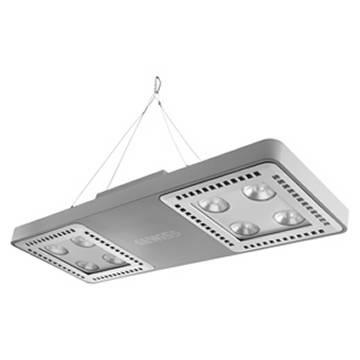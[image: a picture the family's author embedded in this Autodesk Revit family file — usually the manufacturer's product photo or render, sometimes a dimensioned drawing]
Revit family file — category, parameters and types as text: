
# Revit family: Lighting-Industrial-GEWISS-SMART[4]HE_HIGHBAYS-LED_2M
name_source: partatom
category: Apparecchi per illuminazione
units: mm (PartAtom-declared; Revit-internal decimal feet)

## family parameters
Basato su piano di lavoro = Sì
Condiviso = No
Numero OmniClass = 23.80.70.00
Punto di calcolo locali = No
Quota connettore circolare = Usa diametro
Sempre verticale = No
Sorgente d'illuminazione = No
Taglio con vuoti quando caricato = No
Tipo di parte = Normale
Titolo OmniClass = Lighting

## types (36) — shared parameters
Application = Internal
Body = PA6 "Halogen Free" loaded fibreglass
Carico apparente = 97 VA
Catalogue = LIGHTING
Classification: = -
Classificazione = Lighting
Color Rendering Index = CRI-80
Colour = Grey RAL 7035
Colour : = Grey RAL 7035
Commenti sul wattaggio = 97W
Context = Lighting for industries and sports facilities
Control System = ON / OFF
Control System : = ON / OFF
DIN 18032-3 certification = With Bracket - Rope Kit + terminal&nbsp;(in approval)
Device with reduced surface temperature = Yes
Dist_sorg_lum = 10 mm  [stored 0.0328084 ft]
Driver = Included
Driver Box = Built-in
Electrocod = 2444
Eletrical and lighting features = -
External screw = Stainless steel
Fixing = -
Gasket = anti-aging silicone
General information = -
Glow Wire Test : = 850 °C
IDF = 024dbe20-8244-495a-a889-af2c2a435427
IDT = 170d63836ef34e7a91627e9879a3eea4
IP degree = IP66
IPEA = -
Immagine tipo = GWL1311.jpg
Installationa and maintenance = -
Insulation class = I
LED Maintenance = Non-replaceable
Lampada = LED
Larghezza = 254 mm
Lifetime = L90B10 (Tq+25°C) = 70.000 h - L90B10 (Tq+50°C) = 35.000 h
Locking Hook = -
Luminaire = LED Industrial ReflectorÂ
Lunghezza = 699 mm  [stored 2.29331 ft]
Mascherina = <Per categoria>
Materials = -
Maximum surface exposed to the wind : = 0,184 m²
Motore = <Per categoria>
Mouting and installation = Ceiling - Wallmounting - Suspension
Operating temperature : = -30°C ÷ +50 °C
Optic Maintenance = Non-replaceable
Optic and illuminating features = -
Overvoltage protection = DM 6kV / CM 6kV
Photobiological Risk Class = RG0
Produttore = GEWISS S.p.A.
Prospetto di default = 1219 mm
Rated frequency (Hz) = 50/60 Hz
Shield type = Tempered glass Thickness 4mm
Shock resistance = IK08
Spessore plafoniera = 40 mm  [stored 0.131234 ft]
Standard Deviation Colour Matching = SDCM = 3
Standard- = EN 60598-1 ; EN 60598-2-1 ; EN 60598-2-24
Standards and approvals = -
Stocking temperature = -40 +70 °C
Struttura plafoniera = <Per categoria>
Supply voltage = 220 - 240 V
System power = 95W
Technical sheet = https://www.gewiss.com
Tilt- = With bracket accessory
Trasformatore = <Per categoria>
Type of light source = LED - Not replaceable
URL = https://www.gewiss.com
Unique digital code (Datamatrix) = Datamatrix
Version file RFA = 20.11
Voltaggio = 230 V
Warranty = 5 years
Weight (kg): = 6,5
Wiring = With GW connect watertight connector

## per-type parameters (varying)
| type | Colour temperature | Descrizione | Efficiency (lm/W) | Lumen output (lm) | Modello | Optic | Optic : | SEO | Unified Glare Rating |
| GWS4220AF830 - SMART4HB 2M ST.AL.ON/OFF 30° 30K | 3000K | SMART[4]HB 2M ST.AL.ON/OFF 30° 30K | 137 | 13000 | GWS4220AF830 | 30° | Metallic PC reflector and PMMA lenses |  | UGR - 19 |
| GWS4222AC830 - SMART4HB 2M C.PAS.ON/OFF ASI.30K | 3000K | SMART[4]HB 2M C.PAS.ON/OFF ASI.30K | 125 | 11900 | GWS4222AC830 | Asymmetrical | Metallic PC reflector and PMMA lenses | High bay | - |
| GWS4222AC840 - SMART4HB 2M C.PAS.ON/OFF ASI.40K | 4000K | SMART[4]HB 2M C.PAS.ON/OFF ASI.40K | 132 | 12500 | GWS4222AC840 | Asymmetrical | Metallic PC reflector and PMMA lenses | High bay | - |
| GWS4220AP840 - SMART4HB 2M ST.AL.ON/OFF 90° 40K | 4000K | SMART[4]HB 2M ST.AL.ON/OFF 90° 40K | 146 | 13900 | GWS4220AP840 | 90° | Metallic PC reflector and PMMA lenses |  | UGR - 22 |
| GWS4220AH840 - SMART4HB 2M ST.AL.ON/OFF 60° 40K | 4000K | SMART[4]HB 2M ST.AL.ON/OFF 60° 40K | 145 | 13800 | GWS4220AH840 | 60° | Metallic PC reflector and PMMA lenses |  | UGR - 22 |
| GWS4220AC840 - SMART4HB 2M ST.AL.ON/OFF ASI.40K | 4000K | SMART[4]HB 2M ST.AL.ON/OFF ASI.40K | 132 | 12500 | GWS4220AC840 | Asymmetrical | Metallic PC reflector and PMMA lenses | High bay | - |
| GWS4222AA830 - SMART4HB 2M C.PAS.ON/OFF ARR.30K | 3000K | SMART[4]HB 2M C.PAS.ON/OFF ARR.30K | 139 | 13200 | GWS4222AA830 | Array | Metallized polycarbonate reflector |  | UGR - 25 |
| GWS4222AQ830 - SMART4HB 2M C.PAS.ON/OFF ELL.30K | 3000K | SMART[4]HB 2M C.PAS.ON/OFF ELL.30K | 124 | 11800 | GWS4222AQ830 | Elliptical | Metallic PC reflector and PMMA lenses | High bay | - |
| GWS4222AH830 - SMART4HB 2M C.PAS.ON/OFF 60° 30K | 3000K | SMART[4]HB 2M C.PAS.ON/OFF 60° 30K | 138 | 13100 | GWS4222AH830 | 60° | Metallic PC reflector and PMMA lenses |  | UGR - 22 |
| GWS4222AF840 - SMART4HB 2M C.PAS.ON/OFF 30° 40K | 4000K | SMART[4]HB 2M C.PAS.ON/OFF 30° 40K | 144 | 13700 | GWS4222AF840 | 30° | Metallic PC reflector and PMMA lenses |  | UGR - 19 |
| GWS4222AQ857 - SMART4HB 2M C.PAS.ON/OFF ELL.57K | 5700K | SMART[4]HB 2M C.PAS.ON/OFF ELL.57K | 129 | 12300 | GWS4222AQ857 | Elliptical | Metallic PC reflector and PMMA lenses | High bay | - |
| GWS4220AH830 - SMART4HB 2M ST.AL.ON/OFF 60° 30K | 3000K | SMART[4]HB 2M ST.AL.ON/OFF 60° 30K | 138 | 13100 | GWS4220AH830 | 60° | Metallic PC reflector and PMMA lenses |  | UGR - 22 |
| GWS4220AC830 - SMART4HB 2M ST.AL.ON/OFF ASI.30K | 3000K | SMART[4]HB 2M ST.AL.ON/OFF ASI.30K | 125 | 11900 | GWS4220AC830 | Asymmetrical | Metallic PC reflector and PMMA lenses | High bay | - |
| GWS4222AQ840 - SMART4HB 2M C.PAS.ON/OFF ELL.40K | 4000K | SMART[4]HB 2M C.PAS.ON/OFF ELL.40K | 129 | 12300 | GWS4222AQ840 | Elliptical | Metallic PC reflector and PMMA lenses | High bay | - |
| GWS4222AC857 - SMART4HB 2M C.PAS.ON/OFF ASI.57K | 5700K | SMART[4]HB 2M C.PAS.ON/OFF ASI.57K | 132 | 12500 | GWS4222AC857 | Asymmetrical | Metallic PC reflector and PMMA lenses | High bay | - |
| GWS4220AF840 - SMART4HB 2M ST.AL.ON/OFF 30° 40K | 4000K | SMART[4]HB 2M ST.AL.ON/OFF 30° 40K | 144 | 13700 | GWS4220AF840 | 30° | Metallic PC reflector and PMMA lenses |  | UGR - 19 |
| GWS4220AA830 - SMART4HB 2M ST.AL.ON/OFF ARR.30K | 3000K | SMART[4]HB 2M ST.AL.ON/OFF ARR.30K | 139 | 13200 | GWS4220AA830 | Array | Metallized polycarbonate reflector |  | UGR - 25 |
| GWS4220AP857 - SMART4HB 2M ST.AL.ON/OFF 90° 57K | 5700K | SMART[4]HB 2M ST.AL.ON/OFF 90° 57K | 146 | 13900 | GWS4220AP857 | 90° | Metallic PC reflector and PMMA lenses |  | UGR - 22 |
| GWS4222AH857 - SMART4HB 2M C.PAS.ON/OFF 60° 57K | 5700K | SMART[4]HB 2M C.PAS.ON/OFF 60° 57K | 145 | 13800 | GWS4222AH857 | 60° | Metallic PC reflector and PMMA lenses |  | UGR - 22 |
| GWS4220AQ857 - SMART4HB 2M ST.AL.ON/OFF ELL.57K | 5700K | SMART[4]HB 2M ST.AL.ON/OFF ELL.57K | 129 | 12300 | GWS4220AQ857 | Elliptical | Metallic PC reflector and PMMA lenses | High bay | - |
| GWS4222AP857 - SMART4HB 2M C.PAS.ON/OFF 90° 57K | 5700K | SMART[4]HB 2M C.PAS.ON/OFF 90° 57K | 146 | 13900 | GWS4222AP857 | 90° | Metallic PC reflector and PMMA lenses |  | UGR - 22 |
| GWS4220AF857 - SMART4HB 2M ST.AL.ON/OFF 30° 57K | 5700K | SMART[4]HB 2M ST.AL.ON/OFF 30° 57K | 144 | 13700 | GWS4220AF857 | 30° | Metallic PC reflector and PMMA lenses |  | UGR - 19 |
| GWS4220AQ840 - SMART4HB 2M ST.AL.ON/OFF ELL.40K | 4000K | SMART[4]HB 2M ST.AL.ON/OFF ELL.40K | 129 | 12300 | GWS4220AQ840 | Elliptical | Metallic PC reflector and PMMA lenses | High bay | - |
| GWS4222AP840 - SMART4HB 2M C.PAS.ON/OFF 90° 40K | 4000K | SMART[4]HB 2M C.PAS.ON/OFF 90° 40K | 146 | 13900 | GWS4222AP840 | 90° | Metallic PC reflector and PMMA lenses |  | UGR - 22 |
| GWS4220AP830 - SMART4HB 2M ST.AL.ON/OFF 90° 30K | 3000K | SMART[4]HB 2M ST.AL.ON/OFF 90° 30K | 140 | 13300 | GWS4220AP830 | 90° | Metallic PC reflector and PMMA lenses |  | UGR - 22 |
| GWS4222AF830 - SMART4HB 2M C.PAS.ON/OFF 30° 30K | 3000K | SMART[4]HB 2M C.PAS.ON/OFF 30° 30K | 137 | 13000 | GWS4222AF830 | 30° | Metallic PC reflector and PMMA lenses |  | UGR - 19 |
| GWS4220AA857 - SMART4HB 2M ST.AL.ON/OFF ARR.57K | 5700K | SMART[4]HB 2M ST.AL.ON/OFF ARR.57K | 145 | 13800 | GWS4220AA857 | Array | Metallized polycarbonate reflector |  | UGR - 25 |
| GWS4220AH857 - SMART4HB 2M ST.AL.ON/OFF 60° 57K | 5700K | SMART[4]HB 2M ST.AL.ON/OFF 60° 57K | 145 | 13800 | GWS4220AH857 | 60° | Metallic PC reflector and PMMA lenses |  | UGR - 22 |
| GWS4222AA857 - SMART4HB 2M C.PAS.ON/OFF ARR.57K | 5700K | SMART[4]HB 2M C.PAS.ON/OFF ARR.57K | 145 | 13800 | GWS4222AA857 | Array | Metallized polycarbonate reflector |  | UGR - 25 |
| GWS4220AA840 - SMART4HB 2M ST.AL.ON/OFF ARR.40K | 4000K | SMART[4]HB 2M ST.AL.ON/OFF ARR.40K | 145 | 13800 | GWS4220AA840 | Array | Metallized polycarbonate reflector |  | UGR - 25 |
| GWS4222AH840 - SMART4HB 2M C.PAS.ON/OFF 60° 40K | 4000K | SMART[4]HB 2M C.PAS.ON/OFF 60° 40K | 145 | 13800 | GWS4222AH840 | 60° | Metallic PC reflector and PMMA lenses |  | UGR - 22 |
| GWS4220AC857 - SMART4HB 2M ST.AL.ON/OFF ASI.57K | 5700K | SMART[4]HB 2M ST.AL.ON/OFF ASI.57K | 132 | 12500 | GWS4220AC857 | Asymmetrical | Metallic PC reflector and PMMA lenses | High bay | - |
| GWS4222AF857 - SMART4HB 2M C.PAS.ON/OFF 30° 57K | 5700K | SMART[4]HB 2M C.PAS.ON/OFF 30° 57K | 144 | 13700 | GWS4222AF857 | 30° | Metallic PC reflector and PMMA lenses |  | UGR - 19 |
| GWS4220AQ830 - SMART4HB 2M ST.AL.ON/OFF ELL.30K | 3000K | SMART[4]HB 2M ST.AL.ON/OFF ELL.30K | 124 | 11800 | GWS4220AQ830 | Elliptical | Metallic PC reflector and PMMA lenses | High bay | - |
| GWS4222AP830 - SMART4HB 2M C.PAS.ON/OFF 90° 30K | 3000K | SMART[4]HB 2M C.PAS.ON/OFF 90° 30K | 140 | 13300 | GWS4222AP830 | 90° | Metallic PC reflector and PMMA lenses |  | UGR - 22 |
| GWS4222AA840 - SMART4HB 2M C.PAS.ON/OFF ARR.40K | 4000K | SMART[4]HB 2M C.PAS.ON/OFF ARR.40K | 145 | 13800 | GWS4222AA840 | Array | Metallized polycarbonate reflector |  | UGR - 25 |

note: [stored X ft] marks values corroborated as IEEE doubles in the binary element streams (Revit-internal decimal feet)

## geometry (parser evidence)
native form markers: Blend x4, Sweep x3
no freeform markers — native parametric forms only
